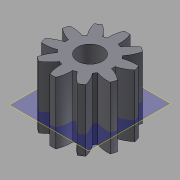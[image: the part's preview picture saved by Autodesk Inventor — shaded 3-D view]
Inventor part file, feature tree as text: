
AUTODESK INVENTOR PART (.ipt)
format: ipt  version: 2015 (Build 190159000, 159)  size: 167,424 bytes
history: native  units: in
note: dims shown in document units (in); Inventor stores cm internally (conversion verified against a paired STEP export)
features: other x13, sketch x3, plane x2
ambient origin geometry x8: Origin, YZ Plane, XZ Plane, XY Plane, X Axis, Y Axis, Z Axis, Center Point
bodies: Solid1 (feature_tree)
feature tree (18):
  other  "Spur Gear19_MIR2.ipt"
  other  "Solid1::Spur Gear19_MIR2.ipt"
  other  "TaggingFeature1"
  sketch  "Sketch1"  dims[d0=0.3937in]
  sketch  "Sketch2"  dims[d16=0.4724in d17=0.0in d41=0.0in d43=0.4724in d46=0.4724in d47=0.0in d48=0.0in]
  sketch  "Sketch3"
  plane  "XZ Plane_1"
  plane  "Work Plane2"
  other  "Z Axis_1"
  other  "Srf1"
  other  "Srf1::Derived"
  other  "Distance iMate"
  other  "Align iMate"
  other  "Mesh iMate"
  other  "Axis iMate"
  other  "Position iMate"
  other  "Mesh iMate2"
  other  "Start plane iMate"
